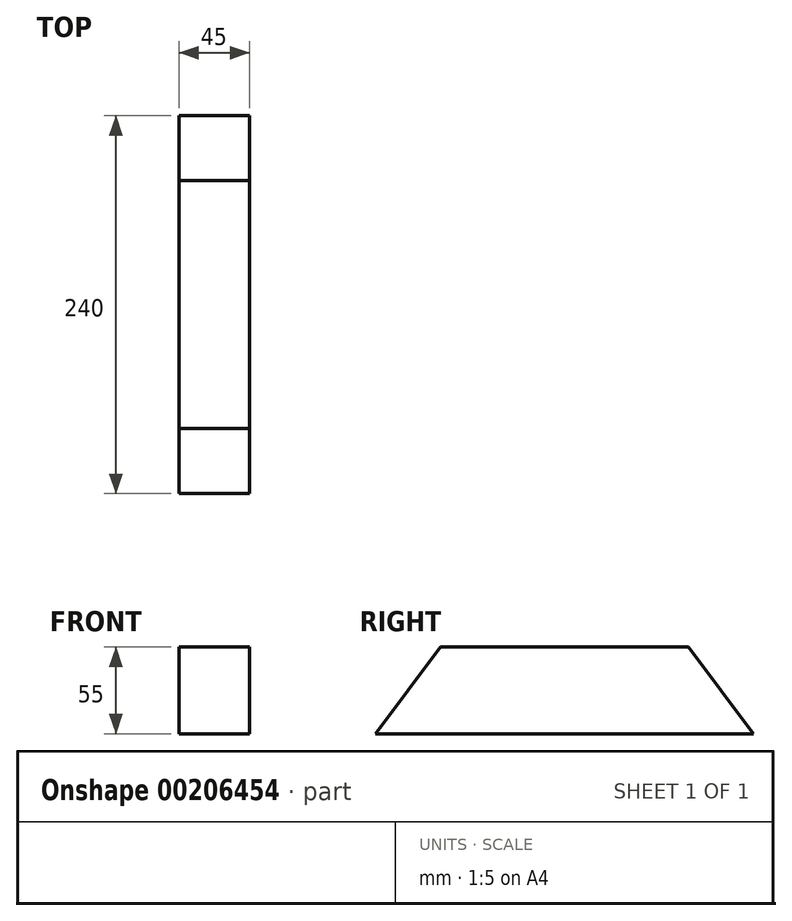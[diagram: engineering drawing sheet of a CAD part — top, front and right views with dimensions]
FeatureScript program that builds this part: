
annotation { "Feature Type Name" : "Feature", "Feature Type Description" : "" }
export const myFeature = defineFeature(function(context is Context, id is Id, definition is map)
    precondition{}
    {
        {
            var Q0;
            Q0=qCreatedBy(makeId("Top.planeOp"),FACE);
            var sketch = newSketch(context, id + "F0", { "sketchPlane" : qUnion([Q0])});
            skLineSegment(sketch, "E0.bottom", {"start": v(17.5, -120) * mm, "end": v(-17.5, -120) * mm});
            skLineSegment(sketch, "E0.top", {"start": v(17.5, 120) * mm, "end": v(-17.5, 120) * mm});
            skLineSegment(sketch, "E0.left", {"start": v(17.5, -120) * mm, "end": v(17.5, 120) * mm});
            skLineSegment(sketch, "E0.right", {"start": v(-17.5, -120) * mm, "end": v(-17.5, 120) * mm});
            skPoint(sketch, "E0.middle", {"position": v(0, 0) * mm});
            skSolve(sketch);
        }
        {
            var Q0;
            Q0 = qSketchRegion(id + "F0", true);
            extrude(context, id + "F1", {"entities" : qUnion([Q0]), "depth" : 3 * mm});
        }
        {
            var Q0;
            Q0=qCreatedBy(makeId("Right.planeOp"),FACE);
            var sketch = newSketch(context, id + "F2", { "sketchPlane" : qUnion([Q0])});
            skLineSegment(sketch, "E1.bottom", {"start": v(-120, 0) * mm, "end": v(120, 0) * mm});
            skLineSegment(sketch, "E1.top", {"start": v(-120, 55) * mm, "end": v(120, 55) * mm});
            skLineSegment(sketch, "E1.left", {"start": v(-120, 0) * mm, "end": v(-120, 55) * mm});
            skLineSegment(sketch, "E1.right", {"start": v(120, 0) * mm, "end": v(120, 55) * mm});
            skSolve(sketch);
        }
        {
            var Q0;
            Q0 = qSketchRegion(id + "F2", true);
            extrude(context, id + "F3", {"entities" : qUnion([Q0]), "operationType" : NewBodyOperationType.ADD, "endBound" : BoundingType.SYMMETRIC, "oppositeDirection" : true, "depth" : 45 * mm});
        }
        {
            var Q0;
            Q0=makeQuery(id+"F3.opExtrude","CAP_FACE",FACE,{"disambiguationData":[OSD([sQuery(id+"F2.wireOp",EDGE,"E1.bottom"),sQuery(id+"F2.wireOp",EDGE,"E1.top"),sQuery(id+"F2.wireOp",EDGE,"E1.left"),sQuery(id+"F2.wireOp",EDGE,"E1.right")])],"isStart":true});
            var sketch = newSketch(context, id + "F4", { "sketchPlane" : qUnion([Q0])});
            skLineSegment(sketch, "E2", {"start": v(-120, 0) * mm, "end": v(-78.7, 55) * mm});
            skLineSegment(sketch, "E3.MirrorCS", {"start": v(120, 0) * mm, "end": v(78.7, 55) * mm});
            skLineSegment(sketch, "E4", {"start": v(-120, 0) * mm, "end": v(-120, 55) * mm});
            skLineSegment(sketch, "E5", {"start": v(-120, 55) * mm, "end": v(-78.7, 55) * mm});
            skLineSegment(sketch, "E6", {"start": v(78.7, 55) * mm, "end": v(120, 55) * mm});
            skLineSegment(sketch, "E7", {"start": v(120, 55) * mm, "end": v(120, 0) * mm});
            skSolve(sketch);
        }
        {
            var Q0;
            Q0=makeQuery(id+"F4.imprint","IMPRINT",FACE,{"disambiguationData":[TD([[makeQuery(id+"F4.imprint","IMPRINT",EDGE,{"derivedFrom":sQuery(id+"F4.wireOp",EDGE,"E2")}),1.0]])]});
            var Q1;
            Q1=makeQuery(id+"F4.imprint","IMPRINT",FACE,{"disambiguationData":[TD([[makeQuery(id+"F4.imprint","IMPRINT",EDGE,{"derivedFrom":sQuery(id+"F4.wireOp",EDGE,"E3.MirrorCS")}),-1.0]])]});
            extrude(context, id + "F5", {"entities" : qUnion([Q0, Q1]), "operationType" : NewBodyOperationType.REMOVE, "endBound" : BoundingType.THROUGH_ALL, "oppositeDirection" : true, "depth" : 25.4 * mm});
        }
    });
